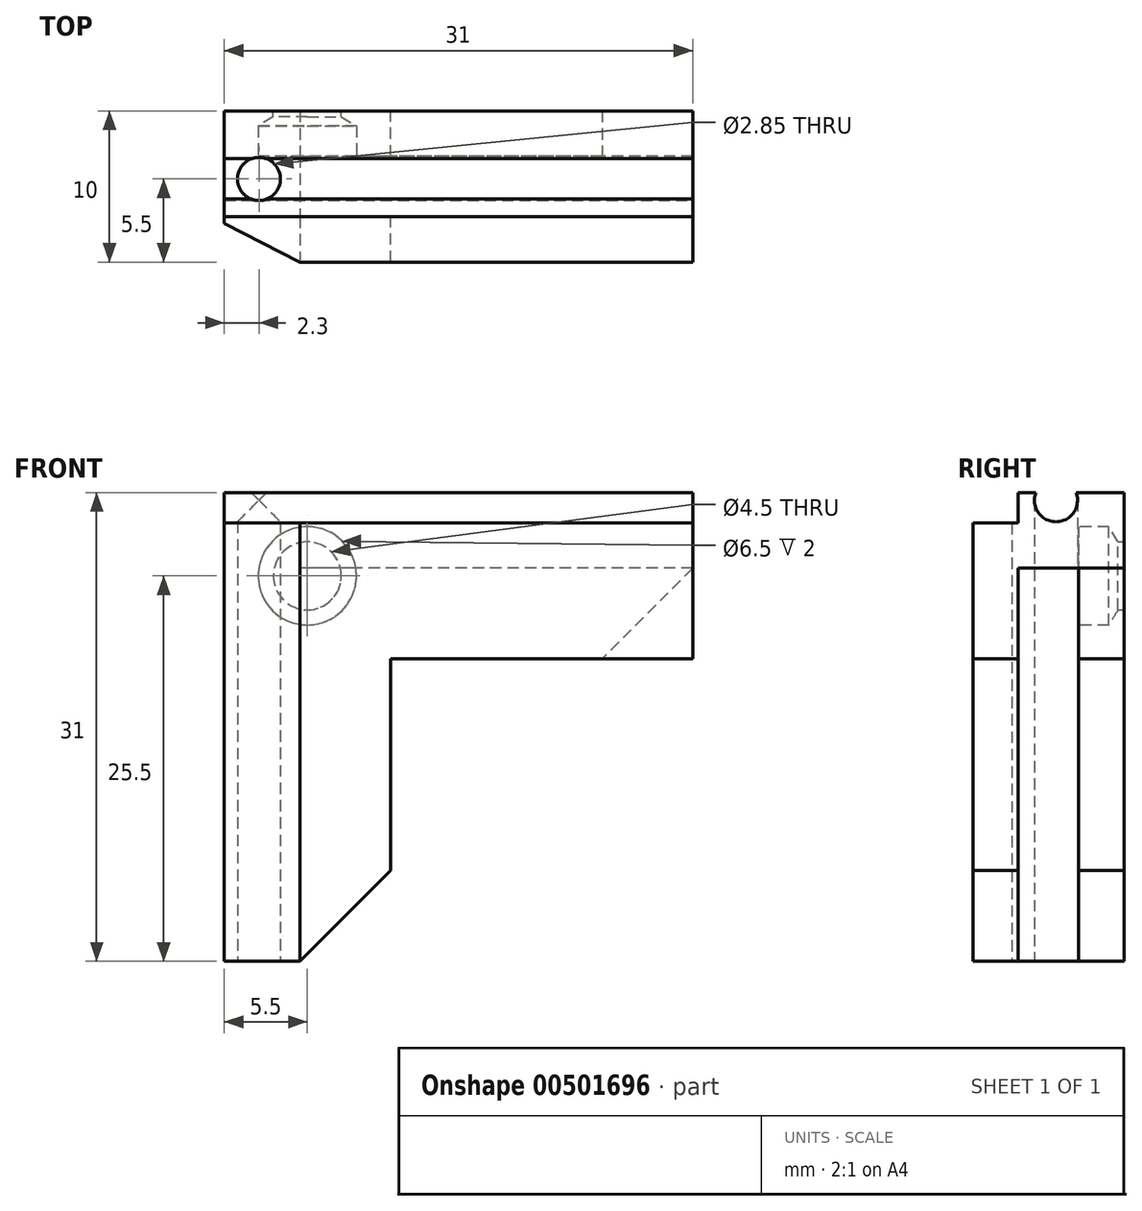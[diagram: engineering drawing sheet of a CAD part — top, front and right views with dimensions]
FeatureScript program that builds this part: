
annotation { "Feature Type Name" : "Feature", "Feature Type Description" : "" }
export const myFeature = defineFeature(function(context is Context, id is Id, definition is map)
    precondition{}
    {
        {
            var Q0;
            Q0=qCreatedBy(makeId("Top.planeOp"),FACE);
            var sketch = newSketch(context, id + "F0", { "sketchPlane" : qUnion([Q0])});
            skLineSegment(sketch, "E0", {"start": v(-12.16, 9.11) * mm, "end": v(-12.16, -0.89) * mm});
            skLineSegment(sketch, "E1", {"start": v(-12.16, -0.89) * mm, "end": v(-3.16, -0.89) * mm});
            skLineSegment(sketch, "E2", {"start": v(-3.16, -0.89) * mm, "end": v(-3.16, 2.11) * mm});
            skLineSegment(sketch, "E3", {"start": v(-3.16, 2.11) * mm, "end": v(-9.16, 2.11) * mm});
            skLineSegment(sketch, "E4", {"start": v(-9.16, 2.11) * mm, "end": v(-9.16, 6.11) * mm});
            skLineSegment(sketch, "E5", {"start": v(-9.16, 6.11) * mm, "end": v(-3.16, 6.11) * mm});
            skLineSegment(sketch, "E6", {"start": v(-3.16, 6.11) * mm, "end": v(-3.16, 9.11) * mm});
            skLineSegment(sketch, "E7", {"start": v(-3.16, 9.11) * mm, "end": v(-12.16, 9.11) * mm});
            skSolve(sketch);
        }
        {
            var Q0;
            Q0=makeQuery(id+"F0.imprint","IMPRINT",FACE,{"disambiguationData":[TD([[makeQuery(id+"F0.imprint","IMPRINT",EDGE,{"derivedFrom":sQuery(id+"F0.wireOp",EDGE,"E0")}),1.0]])]});
            extrude(context, id + "F1", {"entities" : qUnion([Q0]), "depth" : 20 * mm});
        }
        {
            var Q0;
            Q0=makeQuery(id+"F1.opExtrude","SWEPT_FACE",FACE,{"disambiguationData":[OSD([sQuery(id+"F0.wireOp",EDGE,"E0")])]});
            var sketch = newSketch(context, id + "F2", { "sketchPlane" : qUnion([Q0])});
            skLineSegment(sketch, "E8.bottom", {"start": v(-9.11, 20) * mm, "end": v(-2.11, 20) * mm});
            skLineSegment(sketch, "E8.top", {"start": v(-9.11, 0) * mm, "end": v(-2.11, 0) * mm});
            skLineSegment(sketch, "E8.left", {"start": v(-9.11, 20) * mm, "end": v(-9.11, 0) * mm});
            skLineSegment(sketch, "E8.right", {"start": v(-2.11, 20) * mm, "end": v(-2.11, 0) * mm});
            skSolve(sketch);
        }
        {
            var Q0;
            Q0=makeQuery(id+"F2.imprint","IMPRINT",FACE,{"disambiguationData":[TD([[makeQuery(id+"F2.imprint","IMPRINT",EDGE,{"derivedFrom":sQuery(id+"F2.wireOp",EDGE,"E8.bottom")}),-1.0]])]});
            extrude(context, id + "F3", {"entities" : qUnion([Q0]), "operationType" : NewBodyOperationType.ADD, "depth" : 2 * mm});
        }
        {
            var Q0;
            Q0=makeQuery(id+"F1.opExtrude","CAP_FACE",FACE,{"disambiguationData":[OSD([sQuery(id+"F0.wireOp",EDGE,"E0"),sQuery(id+"F0.wireOp",EDGE,"E1"),sQuery(id+"F0.wireOp",EDGE,"E2"),sQuery(id+"F0.wireOp",EDGE,"E3"),sQuery(id+"F0.wireOp",EDGE,"E4"),sQuery(id+"F0.wireOp",EDGE,"E5"),sQuery(id+"F0.wireOp",EDGE,"E6"),sQuery(id+"F0.wireOp",EDGE,"E7")])],"isStart":false});
            var sketch = newSketch(context, id + "F4", { "sketchPlane" : qUnion([Q0])});
            skLineSegment(sketch, "E9", {"start": v(-12.16, 2.11) * mm, "end": v(-12.13, 9.11) * mm});
            skLineSegment(sketch, "E10", {"start": v(-9.16, 9.11) * mm, "end": v(-9.16, -0.89) * mm});
            skSolve(sketch);
        }
        {
            var Q0;
            Q0=makeQuery(id+"F4.imprint","IMPRINT",FACE,{"disambiguationData":[TD([[makeQuery(id+"F4.imprint","IMPRINT",EDGE,{"derivedFrom":sQuery(id+"F4.wireOp",EDGE,"E9")}),-1.0]])]});
            extrude(context, id + "F5", {"entities" : qUnion([Q0]), "operationType" : NewBodyOperationType.ADD, "depth" : 6 * mm});
        }
        {
            var Q0;
            Q0=makeQuery(id+"F5.boolean.opBoolean","MERGE",FACE,{"derivedFrom":[makeQuery(id+"F1.opExtrude","SWEPT_FACE",FACE,{"disambiguationData":[OSD([sQuery(id+"F0.wireOp",EDGE,"E4")])]}),makeQuery(id+"F5.opExtrude","SWEPT_FACE",FACE,{"disambiguationData":[OSD([sQuery(id+"F4.wireOp",EDGE,"E10")])]})]});
            var sketch = newSketch(context, id + "F6", { "sketchPlane" : qUnion([Q0])});
            skLineSegment(sketch, "E11", {"start": v(2.11, 20) * mm, "end": v(2.11, 26) * mm});
            skLineSegment(sketch, "E12", {"start": v(6.11, 20) * mm, "end": v(6.11, 26) * mm});
            skLineSegment(sketch, "E13.bottom", {"start": v(-0.89, 26) * mm, "end": v(9.11, 26) * mm});
            skLineSegment(sketch, "E13.top", {"start": v(-0.89, 29) * mm, "end": v(9.11, 29) * mm});
            skLineSegment(sketch, "E13.left", {"start": v(-0.89, 26) * mm, "end": v(-0.89, 29) * mm});
            skLineSegment(sketch, "E13.right", {"start": v(9.11, 26) * mm, "end": v(9.11, 29) * mm});
            skSolve(sketch);
        }
        {
            var Q0;
            {var subQ0=sQuery(id+"F6.wireOp",EDGE,"E12");Q0=makeQuery(id+"F6.imprint","IMPRINT",FACE,{"disambiguationData":[TD([[makeQuery(id+"F6.imprint","IMPRINT",EDGE,{"derivedFrom":subQ0}),-1.0]])]});}
            var Q1;
            {var subQ0=sQuery(id+"F6.wireOp",EDGE,"E11");Q1=makeQuery(id+"F6.imprint","IMPRINT",FACE,{"disambiguationData":[TD([[makeQuery(id+"F6.imprint","IMPRINT",EDGE,{"derivedFrom":subQ0}),1.0]])]});}
            var Q2;
            Q2=makeQuery(id+"F6.imprint","IMPRINT",FACE,{"disambiguationData":[TD([[makeQuery(id+"F6.imprint","IMPRINT",EDGE,{"derivedFrom":sQuery(id+"F6.wireOp",EDGE,"E13.top")}),-1.0]])]});
            extrude(context, id + "F7", {"entities" : qUnion([Q0, Q1, Q2]), "depth" : 25 * mm});
        }
        {
            var Q0;
            Q0=makeQuery(id+"F5.opExtrude","CAP_FACE",FACE,{"disambiguationData":[OSD([sQuery(id+"F0.wireOp",EDGE,"E0"),sQuery(id+"F0.wireOp",EDGE,"E1"),sQuery(id+"F0.wireOp",EDGE,"E7"),sQuery(id+"F4.wireOp",EDGE,"E9"),sQuery(id+"F4.wireOp",EDGE,"E10")])],"isStart":false});
            extrude(context, id + "F8", {"entities" : qUnion([Q0]), "depth" : 3 * mm});
        }
        {
            var Q0;
            Q0=makeQuery(id+"F7.opExtrude","SWEPT_BODY",BODY,{"disambiguationData":[OSD([sQuery(id+"F0.wireOp",EDGE,"E1"),sQuery(id+"F0.wireOp",EDGE,"E7"),sQuery(id+"F4.wireOp",EDGE,"E10"),sQuery(id+"F6.wireOp",EDGE,"E11"),sQuery(id+"F6.wireOp",EDGE,"E12"),sQuery(id+"F6.wireOp",EDGE,"E13.bottom"),sQuery(id+"F6.wireOp",EDGE,"E13.top"),sQuery(id+"F6.wireOp",EDGE,"E13.left"),sQuery(id+"F6.wireOp",EDGE,"E13.right")])]});
            var Q1;
            Q1=makeQuery(id+"F8.opExtrude","SWEPT_BODY",BODY,{"disambiguationData":[OSD([sQuery(id+"F0.wireOp",EDGE,"E0"),sQuery(id+"F0.wireOp",EDGE,"E1"),sQuery(id+"F0.wireOp",EDGE,"E7"),sQuery(id+"F4.wireOp",EDGE,"E9"),sQuery(id+"F4.wireOp",EDGE,"E10")])]});
            booleanBodies(context, id + "F9", {"operationType" : BooleanOperationType.UNION, "tools" : qUnion([Q0, Q1])});
        }
        {
            var Q0;
            Q0=makeQuery(id+"F7.opExtrude","SWEPT_BODY",BODY,{"disambiguationData":[OSD([sQuery(id+"F0.wireOp",EDGE,"E1"),sQuery(id+"F0.wireOp",EDGE,"E7"),sQuery(id+"F4.wireOp",EDGE,"E10"),sQuery(id+"F6.wireOp",EDGE,"E11"),sQuery(id+"F6.wireOp",EDGE,"E12"),sQuery(id+"F6.wireOp",EDGE,"E13.bottom"),sQuery(id+"F6.wireOp",EDGE,"E13.top"),sQuery(id+"F6.wireOp",EDGE,"E13.left"),sQuery(id+"F6.wireOp",EDGE,"E13.right")])]});
            var Q1;
            Q1=makeQuery(id+"F1.opExtrude","SWEPT_BODY",BODY,{"disambiguationData":[OSD([sQuery(id+"F0.wireOp",EDGE,"E0"),sQuery(id+"F0.wireOp",EDGE,"E1"),sQuery(id+"F0.wireOp",EDGE,"E2"),sQuery(id+"F0.wireOp",EDGE,"E3"),sQuery(id+"F0.wireOp",EDGE,"E4"),sQuery(id+"F0.wireOp",EDGE,"E5"),sQuery(id+"F0.wireOp",EDGE,"E6"),sQuery(id+"F0.wireOp",EDGE,"E7")])]});
            booleanBodies(context, id + "F10", {"operationType" : BooleanOperationType.UNION, "tools" : qUnion([Q0, Q1])});
        }
        {
            var Q0;
            Q0=makeQuery(id+"F9.opBoolean","MERGE",FACE,{"derivedFrom":[makeQuery(id+"F7.opExtrude","SWEPT_FACE",FACE,{"disambiguationData":[OSD([sQuery(id+"F6.wireOp",EDGE,"E13.top")])]}),makeQuery(id+"F8.opExtrude","CAP_FACE",FACE,{"disambiguationData":[OSD([sQuery(id+"F0.wireOp",EDGE,"E0"),sQuery(id+"F0.wireOp",EDGE,"E1"),sQuery(id+"F0.wireOp",EDGE,"E7"),sQuery(id+"F4.wireOp",EDGE,"E9"),sQuery(id+"F4.wireOp",EDGE,"E10")])],"isStart":false})]});
            var sketch = newSketch(context, id + "F11", { "sketchPlane" : qUnion([Q0])});
            skLineSegment(sketch, "E14.bottom", {"start": v(-12.16, 2.11) * mm, "end": v(15.84, 2.11) * mm});
            skLineSegment(sketch, "E14.top", {"start": v(-12.16, 9.11) * mm, "end": v(15.84, 9.11) * mm});
            skLineSegment(sketch, "E14.left", {"start": v(-12.16, 2.11) * mm, "end": v(-12.16, 9.11) * mm});
            skLineSegment(sketch, "E14.right", {"start": v(15.84, 2.11) * mm, "end": v(15.84, 9.11) * mm});
            skSolve(sketch);
        }
        {
            var Q0;
            Q0=makeQuery(id+"F11.imprint","IMPRINT",FACE,{"disambiguationData":[TD([[makeQuery(id+"F11.imprint","IMPRINT",EDGE,{"derivedFrom":sQuery(id+"F11.wireOp",EDGE,"E14.bottom")}),1.0]])]});
            extrude(context, id + "F12", {"entities" : qUnion([Q0]), "operationType" : NewBodyOperationType.ADD, "depth" : 2 * mm});
        }
        {
            var Q0;
            Q0=makeQuery(id+"F4.imprint","IMPRINT",FACE,{"disambiguationData":[TD([[makeQuery(id+"F4.imprint","IMPRINT",EDGE,{"derivedFrom":sQuery(id+"F4.wireOp",EDGE,"E9")}),1.0]])]});
            extrude(context, id + "F13", {"entities" : qUnion([Q0]), "operationType" : NewBodyOperationType.ADD, "depth" : 11 * mm});
        }
        {
            var Q0;
            {var subQ0=sQuery(id+"F2.wireOp",EDGE,"E8.right");Q0=makeQuery(id+"F13.boolean.opBoolean","MERGE",EDGE,{"derivedFrom":[makeQuery(id+"F3.opExtrude","CAP_EDGE",EDGE,{"disambiguationData":[OSD([subQ0])],"isStart":true}),makeQuery(id+"F13.opExtrude","SWEPT_EDGE",EDGE,{"disambiguationData":[OSD([sQuery(id+"F0.wireOp",EDGE,"E0"),sQuery(id+"F2.wireOp",EDGE,"E8.bottom"),subQ0,sQuery(id+"F4.wireOp",EDGE,"E9")])]})]});}
            var Q1;
            Q1=makeQuery(id+"F12.opExtrude","CAP_EDGE",EDGE,{"disambiguationData":[OSD([sQuery(id+"F11.wireOp",EDGE,"E14.bottom")])],"isStart":true});
            chamfer(context, id + "F14", {"entities" : qUnion([Q0, Q1]), "width" : 4 * mm, "tangentPropagation" : true});
        }
        {
            var Q0;
            {var subQ0=sQuery(id+"F0.wireOp",EDGE,"E1");var subQ1=sQuery(id+"F2.wireOp",EDGE,"E8.right");Q0=makeQuery(id+"F14.opChamfer","BLEND_EDGE",EDGE,{"blendedFrom":[makeQuery(id+"F13.boolean.opBoolean","MERGE",EDGE,{"derivedFrom":[makeQuery(id+"F3.opExtrude","CAP_EDGE",EDGE,{"disambiguationData":[OSD([subQ1])],"isStart":true}),makeQuery(id+"F13.opExtrude","SWEPT_EDGE",EDGE,{"disambiguationData":[OSD([sQuery(id+"F0.wireOp",EDGE,"E0"),sQuery(id+"F2.wireOp",EDGE,"E8.bottom"),subQ1,sQuery(id+"F4.wireOp",EDGE,"E9")])]})]}),makeQuery(id+"F10.opBoolean","MERGE",FACE,{"derivedFrom":[makeQuery(id+"F5.boolean.opBoolean","MERGE",FACE,{"derivedFrom":[makeQuery(id+"F1.opExtrude","SWEPT_FACE",FACE,{"disambiguationData":[OSD([subQ0])]}),makeQuery(id+"F5.opExtrude","SWEPT_FACE",FACE,{"disambiguationData":[OSD([subQ0])]})]}),makeQuery(id+"F9.opBoolean","MERGE",FACE,{"derivedFrom":[makeQuery(id+"F7.opExtrude","SWEPT_FACE",FACE,{"disambiguationData":[OSD([subQ0,sQuery(id+"F4.wireOp",EDGE,"E10"),sQuery(id+"F6.wireOp",EDGE,"E13.left")])]}),makeQuery(id+"F8.opExtrude","SWEPT_FACE",FACE,{"disambiguationData":[OSD([subQ0])]})]})]})],"blendedInto":[makeQuery(id+"F10.opBoolean","MERGE",FACE,{"derivedFrom":[makeQuery(id+"F5.boolean.opBoolean","MERGE",FACE,{"derivedFrom":[makeQuery(id+"F1.opExtrude","SWEPT_FACE",FACE,{"disambiguationData":[OSD([subQ0])]}),makeQuery(id+"F5.opExtrude","SWEPT_FACE",FACE,{"disambiguationData":[OSD([subQ0])]})]}),makeQuery(id+"F9.opBoolean","MERGE",FACE,{"derivedFrom":[makeQuery(id+"F7.opExtrude","SWEPT_FACE",FACE,{"disambiguationData":[OSD([subQ0,sQuery(id+"F4.wireOp",EDGE,"E10"),sQuery(id+"F6.wireOp",EDGE,"E13.left")])]}),makeQuery(id+"F8.opExtrude","SWEPT_FACE",FACE,{"disambiguationData":[OSD([subQ0])]})]})]})]});}
            var Q1;
            {var subQ0=sQuery(id+"F0.wireOp",EDGE,"E1");Q1=makeQuery(id+"F14.opChamfer","BLEND_EDGE",EDGE,{"blendedFrom":[makeQuery(id+"F12.opExtrude","CAP_EDGE",EDGE,{"disambiguationData":[OSD([sQuery(id+"F11.wireOp",EDGE,"E14.bottom")])],"isStart":true}),makeQuery(id+"F10.opBoolean","MERGE",FACE,{"derivedFrom":[makeQuery(id+"F5.boolean.opBoolean","MERGE",FACE,{"derivedFrom":[makeQuery(id+"F1.opExtrude","SWEPT_FACE",FACE,{"disambiguationData":[OSD([subQ0])]}),makeQuery(id+"F5.opExtrude","SWEPT_FACE",FACE,{"disambiguationData":[OSD([subQ0])]})]}),makeQuery(id+"F9.opBoolean","MERGE",FACE,{"derivedFrom":[makeQuery(id+"F7.opExtrude","SWEPT_FACE",FACE,{"disambiguationData":[OSD([subQ0,sQuery(id+"F4.wireOp",EDGE,"E10"),sQuery(id+"F6.wireOp",EDGE,"E13.left")])]}),makeQuery(id+"F8.opExtrude","SWEPT_FACE",FACE,{"disambiguationData":[OSD([subQ0])]})]})]})],"blendedInto":[makeQuery(id+"F10.opBoolean","MERGE",FACE,{"derivedFrom":[makeQuery(id+"F5.boolean.opBoolean","MERGE",FACE,{"derivedFrom":[makeQuery(id+"F1.opExtrude","SWEPT_FACE",FACE,{"disambiguationData":[OSD([subQ0])]}),makeQuery(id+"F5.opExtrude","SWEPT_FACE",FACE,{"disambiguationData":[OSD([subQ0])]})]}),makeQuery(id+"F9.opBoolean","MERGE",FACE,{"derivedFrom":[makeQuery(id+"F7.opExtrude","SWEPT_FACE",FACE,{"disambiguationData":[OSD([subQ0,sQuery(id+"F4.wireOp",EDGE,"E10"),sQuery(id+"F6.wireOp",EDGE,"E13.left")])]}),makeQuery(id+"F8.opExtrude","SWEPT_FACE",FACE,{"disambiguationData":[OSD([subQ0])]})]})]})]});}
            chamfer(context, id + "F15", {"entities" : qUnion([Q0, Q1]), "chamferType" : ChamferType.TWO_OFFSETS, "width1" : 4 * mm, "oppositeDirection" : false, "width2" : 6 * mm, "tangentPropagation" : true});
        }
        {
            var Q0;
            Q0=makeQuery(id+"F12.boolean.opBoolean","MERGE",FACE,{"derivedFrom":[makeQuery(id+"F7.opExtrude","CAP_FACE",FACE,{"disambiguationData":[OSD([sQuery(id+"F0.wireOp",EDGE,"E1"),sQuery(id+"F0.wireOp",EDGE,"E7"),sQuery(id+"F4.wireOp",EDGE,"E10"),sQuery(id+"F6.wireOp",EDGE,"E11"),sQuery(id+"F6.wireOp",EDGE,"E12"),sQuery(id+"F6.wireOp",EDGE,"E13.bottom"),sQuery(id+"F6.wireOp",EDGE,"E13.top"),sQuery(id+"F6.wireOp",EDGE,"E13.left"),sQuery(id+"F6.wireOp",EDGE,"E13.right")])],"isStart":false}),makeQuery(id+"F12.opExtrude","SWEPT_FACE",FACE,{"disambiguationData":[OSD([sQuery(id+"F11.wireOp",EDGE,"E14.right")])]})]});
            extrude(context, id + "F16", {"entities" : qUnion([Q0]), "operationType" : NewBodyOperationType.ADD, "depth" : 1 * mm});
        }
        {
            var Q0;
            {var subQ2=sQuery(id+"F0.wireOp",EDGE,"E1");var subQ3=sQuery(id+"F4.wireOp",EDGE,"E10");Q0=makeQuery(id+"F16.opExtrude","CAP_EDGE",EDGE,{"disambiguationData":[OSD([subQ3]),TDD([makeQuery(id+"F7.opExtrude","CAP_EDGE",EDGE,{"disambiguationData":[OSD([subQ3]),TDD([makeQuery(id+"F6.imprint","IMPRINT",EDGE,{"derivedFrom":makeQuery(id+"F5.boolean.opBoolean","SPLIT",EDGE,{"disambiguationData":[TD([makeQuery(id+"F1.opExtrude","SWEPT_FACE",FACE,{"disambiguationData":[OSD([subQ2])]})])],"derivedFrom":makeQuery(id+"F5.opExtrude","CAP_EDGE",EDGE,{"disambiguationData":[OSD([subQ3])],"isStart":true})})})])],"isStart":false})])],"isStart":false});}
            var Q1;
            {var subQ1=sQuery(id+"F4.wireOp",EDGE,"E10");var subQ3=sQuery(id+"F0.wireOp",EDGE,"E5");Q1=makeQuery(id+"F16.opExtrude","CAP_EDGE",EDGE,{"disambiguationData":[OSD([subQ1]),TDD([makeQuery(id+"F7.opExtrude","CAP_EDGE",EDGE,{"disambiguationData":[OSD([subQ1]),TDD([makeQuery(id+"F6.imprint","IMPRINT",EDGE,{"derivedFrom":makeQuery(id+"F5.boolean.opBoolean","SPLIT",EDGE,{"disambiguationData":[TD([makeQuery(id+"F1.opExtrude","SWEPT_FACE",FACE,{"disambiguationData":[OSD([subQ3])]})])],"derivedFrom":makeQuery(id+"F5.opExtrude","CAP_EDGE",EDGE,{"disambiguationData":[OSD([subQ1])],"isStart":true})})})])],"isStart":false})])],"isStart":false});}
            var Q2;
            Q2=makeQuery(id+"F1.opExtrude","CAP_EDGE",EDGE,{"disambiguationData":[OSD([sQuery(id+"F0.wireOp",EDGE,"E2")])],"isStart":true});
            var Q3;
            Q3=makeQuery(id+"F1.opExtrude","CAP_EDGE",EDGE,{"disambiguationData":[OSD([sQuery(id+"F0.wireOp",EDGE,"E6")])],"isStart":true});
            chamfer(context, id + "F17", {"entities" : qUnion([Q0, Q1, Q2, Q3]), "width" : 6 * mm, "tangentPropagation" : true});
        }
        {
            var Q0;
            Q0=makeQuery(id+"F16.opExtrude","CAP_FACE",FACE,{"disambiguationData":[OSD([sQuery(id+"F0.wireOp",EDGE,"E1"),sQuery(id+"F0.wireOp",EDGE,"E7"),sQuery(id+"F2.wireOp",EDGE,"E8.bottom"),sQuery(id+"F2.wireOp",EDGE,"E8.left"),sQuery(id+"F4.wireOp",EDGE,"E10"),sQuery(id+"F6.wireOp",EDGE,"E11"),sQuery(id+"F6.wireOp",EDGE,"E12"),sQuery(id+"F6.wireOp",EDGE,"E13.bottom"),sQuery(id+"F6.wireOp",EDGE,"E13.top"),sQuery(id+"F6.wireOp",EDGE,"E13.left"),sQuery(id+"F6.wireOp",EDGE,"E13.right"),sQuery(id+"F11.wireOp",EDGE,"E14.right")])],"isStart":false});
            var sketch = newSketch(context, id + "F18", { "sketchPlane" : qUnion([Q0])});
            skPoint(sketch, "E15", {"position": v(4.61, 30.5) * mm});
            skSolve(sketch);
        }
        {
            var Q0;
            Q0=makeQuery(id+"F3.boolean.opBoolean","MERGE",FACE,{"derivedFrom":[makeQuery(id+"F1.opExtrude","CAP_FACE",FACE,{"disambiguationData":[OSD([sQuery(id+"F0.wireOp",EDGE,"E0"),sQuery(id+"F0.wireOp",EDGE,"E1"),sQuery(id+"F0.wireOp",EDGE,"E2"),sQuery(id+"F0.wireOp",EDGE,"E3"),sQuery(id+"F0.wireOp",EDGE,"E4"),sQuery(id+"F0.wireOp",EDGE,"E5"),sQuery(id+"F0.wireOp",EDGE,"E6"),sQuery(id+"F0.wireOp",EDGE,"E7")])],"isStart":true}),makeQuery(id+"F3.opExtrude","SWEPT_FACE",FACE,{"disambiguationData":[OSD([sQuery(id+"F2.wireOp",EDGE,"E8.top")])]})]});
            var sketch = newSketch(context, id + "F19", { "sketchPlane" : qUnion([Q0])});
            skPoint(sketch, "E16", {"position": v(-11.86, -4.61) * mm});
            skSolve(sketch);
        }
        {
            var Q0;
            Q0=sQuery(id+"F19.wireOp",VERTEX,"E16");
            var Q1;
            Q1=sQuery(id+"F18.wireOp",VERTEX,"E15");
            var Q2;
            Q2=makeQuery(id+"F7.opExtrude","SWEPT_BODY",BODY,{"disambiguationData":[OSD([sQuery(id+"F0.wireOp",EDGE,"E1"),sQuery(id+"F0.wireOp",EDGE,"E7"),sQuery(id+"F2.wireOp",EDGE,"E8.bottom"),sQuery(id+"F2.wireOp",EDGE,"E8.left"),sQuery(id+"F4.wireOp",EDGE,"E10"),sQuery(id+"F6.wireOp",EDGE,"E11"),sQuery(id+"F6.wireOp",EDGE,"E12"),sQuery(id+"F6.wireOp",EDGE,"E13.bottom"),sQuery(id+"F6.wireOp",EDGE,"E13.top"),sQuery(id+"F6.wireOp",EDGE,"E13.left"),sQuery(id+"F6.wireOp",EDGE,"E13.right")])]});
            hole(context, id + "F20", {"style" : HoleStyle.SIMPLE, "endStyle" : HoleEndStyle.THROUGH, "holeDiameter" : 2.85 * mm, "isTappedThrough" : true, "tappedDepth" : 12 * mm, "tapClearance" : 3, "locations" : qUnion([Q0, Q1]), "scope" : qUnion([Q2])});
        }
        {
            var Q0;
            {var subQ0=sQuery(id+"F11.wireOp",EDGE,"E14.top");var subQ1=sQuery(id+"F6.wireOp",EDGE,"E13.right");var subQ2=sQuery(id+"F4.wireOp",EDGE,"E10");var subQ3=sQuery(id+"F2.wireOp",EDGE,"E8.left");var subQ4=sQuery(id+"F2.wireOp",EDGE,"E8.bottom");var subQ5=sQuery(id+"F0.wireOp",EDGE,"E7");Q0=makeQuery(id+"F16.boolean.opBoolean","MERGE",FACE,{"derivedFrom":[makeQuery(id+"F13.boolean.opBoolean","MERGE",FACE,{"derivedFrom":[makeQuery(id+"F12.boolean.opBoolean","MERGE",FACE,{"derivedFrom":[makeQuery(id+"F10.opBoolean","MERGE",FACE,{"derivedFrom":[makeQuery(id+"F5.boolean.opBoolean","MERGE",FACE,{"derivedFrom":[makeQuery(id+"F3.boolean.opBoolean","MERGE",FACE,{"derivedFrom":[makeQuery(id+"F1.opExtrude","SWEPT_FACE",FACE,{"disambiguationData":[OSD([subQ5])]}),makeQuery(id+"F3.opExtrude","SWEPT_FACE",FACE,{"disambiguationData":[OSD([subQ3])]})]}),makeQuery(id+"F5.opExtrude","SWEPT_FACE",FACE,{"disambiguationData":[OSD([subQ5,subQ4,subQ3])]})]}),makeQuery(id+"F9.opBoolean","MERGE",FACE,{"derivedFrom":[makeQuery(id+"F7.opExtrude","SWEPT_FACE",FACE,{"disambiguationData":[OSD([subQ5,subQ4,subQ3,subQ2,subQ1])]}),makeQuery(id+"F8.opExtrude","SWEPT_FACE",FACE,{"disambiguationData":[OSD([subQ5,subQ4,subQ3])]})]})]}),makeQuery(id+"F12.opExtrude","SWEPT_FACE",FACE,{"disambiguationData":[OSD([subQ0])]})]}),makeQuery(id+"F13.opExtrude","SWEPT_FACE",FACE,{"disambiguationData":[OSD([subQ5,subQ4,subQ3])]})]}),makeQuery(id+"F16.opExtrude","SWEPT_FACE",FACE,{"disambiguationData":[OSD([subQ5,subQ4,subQ3,subQ2,subQ1,subQ0,sQuery(id+"F11.wireOp",EDGE,"E14.right")])]})]});}
            var sketch = newSketch(context, id + "F21", { "sketchPlane" : qUnion([Q0])});
            skLineSegment(sketch, "E17", {"start": v(3.16, 20) * mm, "end": v(14.16, 31) * mm});
            skPoint(sketch, "E18", {"position": v(8.66, 25.5) * mm});
            skCircle(sketch, "E19", {"center": v(8.66, 25.5) * mm, "radius": 2.25 * mm});
            skSolve(sketch);
        }
        {
            var Q0;
            {var subQ0=sQuery(id+"F21.wireOp",EDGE,"E19");var subQ1=sQuery(id+"F21.wireOp",EDGE,"E17");var subQ2=makeQuery(id+"F21.imprint","INTERSECT",VERTEX,{"disambiguationData":[OD(0.0)],"derivedFrom":[subQ1,subQ0]});Q0=makeQuery(id+"F21.imprint","IMPRINT",FACE,{"disambiguationData":[TD([[makeQuery(id+"F21.imprint","IMPRINT",EDGE,{"disambiguationData":[TD([[subQ2,-1.0]])],"derivedFrom":subQ1}),-1.0]])]});}
            var Q1;
            {var subQ0=sQuery(id+"F21.wireOp",EDGE,"E19");var subQ1=sQuery(id+"F21.wireOp",EDGE,"E17");var subQ2=makeQuery(id+"F21.imprint","INTERSECT",VERTEX,{"disambiguationData":[OD(0.0)],"derivedFrom":[subQ1,subQ0]});Q1=makeQuery(id+"F21.imprint","IMPRINT",FACE,{"disambiguationData":[TD([[makeQuery(id+"F21.imprint","IMPRINT",EDGE,{"disambiguationData":[TD([[subQ2,-1.0]])],"derivedFrom":subQ1}),1.0]])]});}
            extrude(context, id + "F22", {"entities" : qUnion([Q0, Q1]), "operationType" : NewBodyOperationType.REMOVE, "oppositeDirection" : true, "depth" : 3 * mm, "offsetDistance" : 25 * mm});
        }
        {
            var Q0;
            Q0=makeQuery(id+"F22.boolean.opBoolean","COPY",FACE,{"derivedFrom":makeQuery(id+"F22.opExtrude","CAP_FACE",FACE,{"disambiguationData":[OSD([sQuery(id+"F21.wireOp",EDGE,"E19")])],"isStart":false})});
            var sketch = newSketch(context, id + "F23", { "sketchPlane" : qUnion([Q0])});
            skPoint(sketch, "E20", {"position": v(8.66, 25.5) * mm});
            skSolve(sketch);
        }
        {
            var Q0;
            Q0=sQuery(id+"F23.wireOp",VERTEX,"E20");
            var Q1;
            Q1=makeQuery(id+"F7.opExtrude","SWEPT_BODY",BODY,{"disambiguationData":[OSD([sQuery(id+"F0.wireOp",EDGE,"E1"),sQuery(id+"F0.wireOp",EDGE,"E7"),sQuery(id+"F2.wireOp",EDGE,"E8.bottom"),sQuery(id+"F2.wireOp",EDGE,"E8.left"),sQuery(id+"F4.wireOp",EDGE,"E10"),sQuery(id+"F6.wireOp",EDGE,"E11"),sQuery(id+"F6.wireOp",EDGE,"E12"),sQuery(id+"F6.wireOp",EDGE,"E13.bottom"),sQuery(id+"F6.wireOp",EDGE,"E13.top"),sQuery(id+"F6.wireOp",EDGE,"E13.left"),sQuery(id+"F6.wireOp",EDGE,"E13.right")])]});
            hole(context, id + "F24", {"style" : HoleStyle.SIMPLE, "endStyle" : HoleEndStyle.BLIND, "oppositeDirection" : true, "holeDiameter" : 6.5 * mm, "holeDepth" : 2 * mm, "isTappedThrough" : true, "tappedDepth" : 12 * mm, "tapClearance" : 3, "locations" : qUnion([Q0]), "scope" : qUnion([Q1])});
        }
    });
